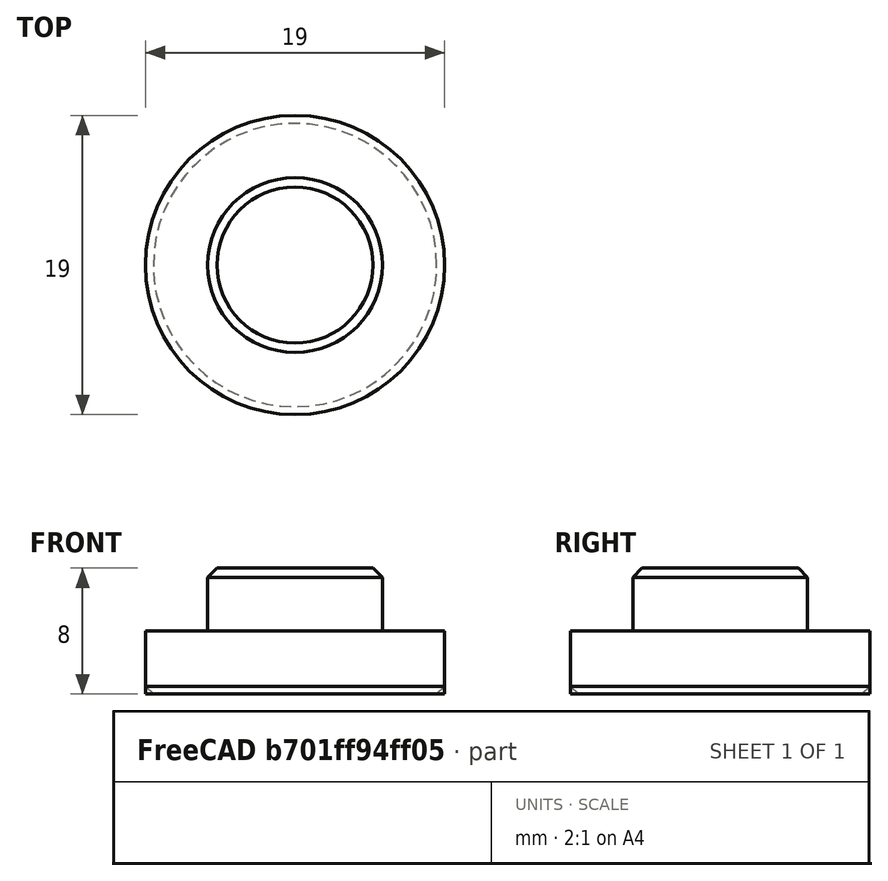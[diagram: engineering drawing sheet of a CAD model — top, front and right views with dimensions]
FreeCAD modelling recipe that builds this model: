
FCSTD DOCUMENT  (FreeCAD 0.16R)
Label: RTBushing22
License: All rights reserved
LicenseURL: http://en.wikipedia.org/wiki/All_rights_reserved
objects: Sketcher::SketchObject×3, PartDesign::Pad×2, PartDesign::Chamfer×2, Mesh::Feature×1
note: 9 computed .brp shape members not serialized (recipe doc carries the construction recipe); baked Part::Feature solids carry a one-line shape summary decoded from their .brp

FEATURE [Sketcher::SketchObject] Sketch
  sketch-geometry (1):
    g0: Circle CenterX=0 CenterY=0 CenterZ=0 NormalX=0 NormalY=0 NormalZ=1 Radius=9.5
  constraints (2):
    c: Coincident(g0,g-1)
    c: Radius(g0) = 9.5
FEATURE [PartDesign::Pad] Pad
  Length = 4
  Length2 = 100
  Sketch = -> Sketch
  Type = 0
FEATURE [Sketcher::SketchObject] Sketch001
  Placement = pos=(0,0,4) rot=(0,0,1;0rad)
  Support = -> Pad [Face3]
  sketch-geometry (1):
    g0: Circle CenterX=0 CenterY=0 CenterZ=0 NormalX=0 NormalY=0 NormalZ=1 Radius=5.55
  constraints (2):
    c: Coincident(g0,g-1)
    c: Radius(g0) = 5.55
FEATURE [PartDesign::Pad] Pad001
  Length = 4
  Length2 = 100
  Sketch = -> Sketch001
  Type = 0
FEATURE [Sketcher::SketchObject] Sketch002
  Placement = pos=(0,0,8) rot=(0,0,1;0rad)
  Support = -> Pad001 [Face5]
  sketch-geometry (1):
    g0: Circle CenterX=0 CenterY=0 CenterZ=0 NormalX=0 NormalY=0 NormalZ=1 Radius=3.75
  constraints (2):
    c: Coincident(g0,g-1)
    c: Radius(g0) = 3.75
FEATURE [PartDesign::Chamfer] Chamfer
  Base = -> Pad001 [Edge2]
  Size = 0.5
FEATURE [PartDesign::Chamfer] Chamfer001
  Base = -> Chamfer [Edge8]
  Size = 0.59
FEATURE [Mesh::Feature] Mesh  label="Chamfer001 (Meshed)"
